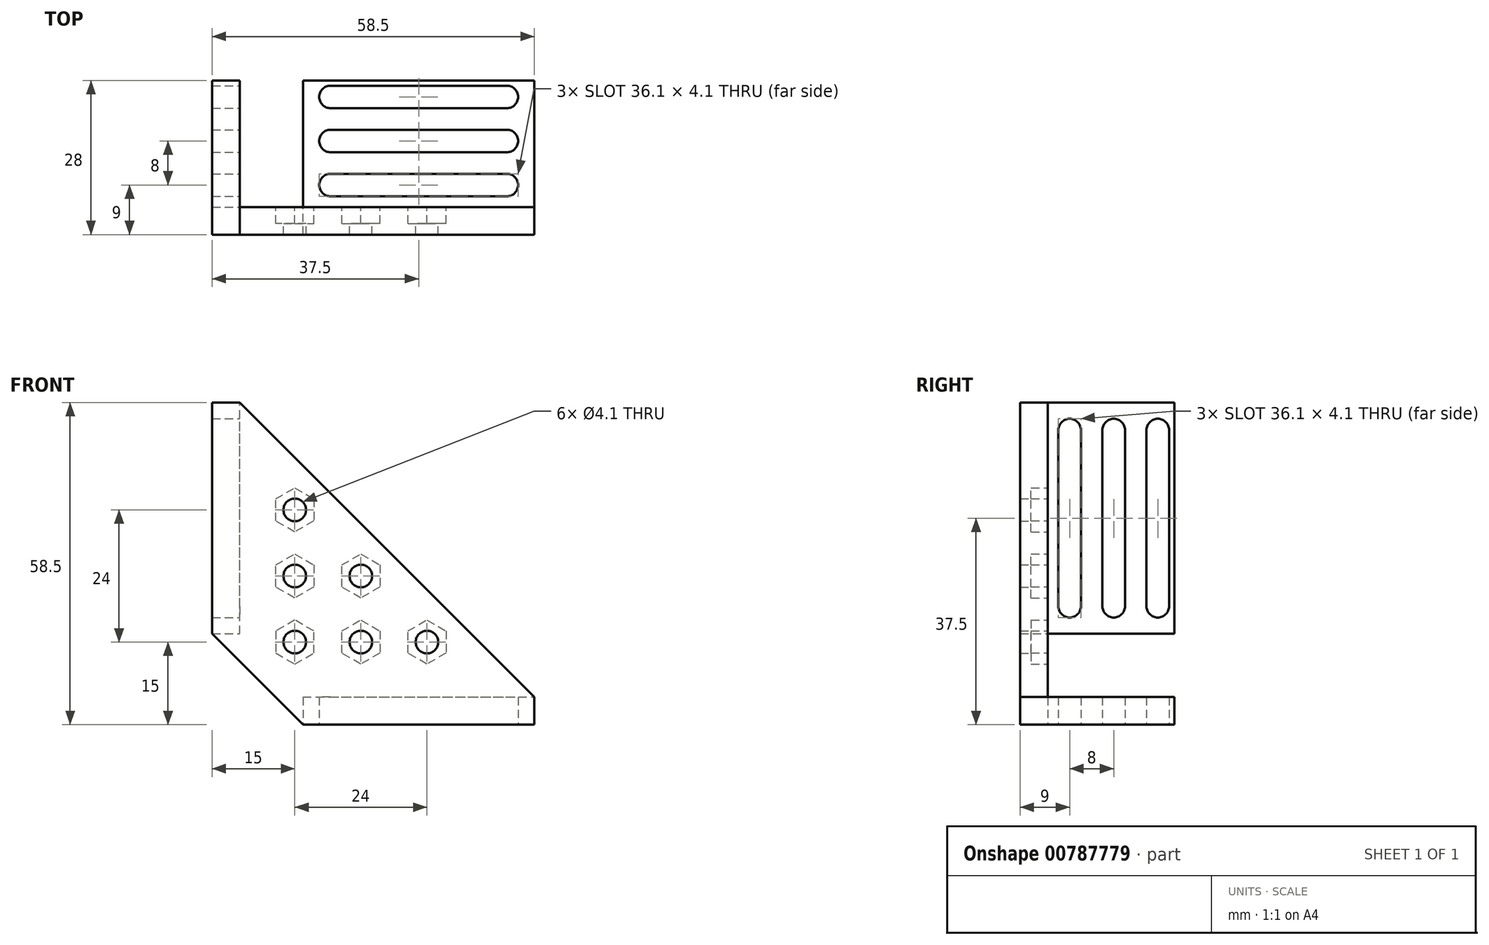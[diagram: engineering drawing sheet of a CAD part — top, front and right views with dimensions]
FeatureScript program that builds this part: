
annotation { "Feature Type Name" : "Feature", "Feature Type Description" : "" }
export const myFeature = defineFeature(function(context is Context, id is Id, definition is map)
    precondition{}
    {
        {
            var Q0;
            Q0=qCreatedBy(makeId("Top.planeOp"),FACE);
            var sketch = newSketch(context, id + "F0", { "sketchPlane" : qUnion([Q0])});
            skLineSegment(sketch, "E0.bottom", {"start": v(-21, 11.5) * mm, "end": v(21, 11.5) * mm});
            skLineSegment(sketch, "E0.top", {"start": v(-21, -11.5) * mm, "end": v(21, -11.5) * mm});
            skLineSegment(sketch, "E0.left", {"start": v(-21, 11.5) * mm, "end": v(-21, -11.5) * mm});
            skLineSegment(sketch, "E0.right", {"start": v(21, 11.5) * mm, "end": v(21, -11.5) * mm});
            skPoint(sketch, "E0.middle", {"position": v(0, 0) * mm});
            skLineSegment(sketch, "E1", {"start": v(0, 11.5) * mm, "end": v(0, -11.5) * mm, "construction": true});
            skLineSegment(sketch, "E2", {"start": v(-21, -7.5) * mm, "end": v(21, -7.5) * mm, "construction": true});
            skLineSegment(sketch, "E3", {"start": v(-16, 11.5) * mm, "end": v(-16, -11.5) * mm, "construction": true});
            skPoint(sketch, "E4", {"position": v(-16, -7.5) * mm});
            skPoint(sketch, "E5", {"position": v(0, -7.5) * mm});
            skArc(sketch, "E6", {"start": v(-16, -5.45) * mm, "mid": v(-18.05, -7.5) * mm, "end": v(-16, -9.55) * mm});
            skArc(sketch, "E7.MirrorCS", {"start": v(16, -5.45) * mm, "mid": v(18.05, -7.5) * mm, "end": v(16, -9.55) * mm});
            skLineSegment(sketch, "E8", {"start": v(-16, -5.45) * mm, "end": v(16, -5.45) * mm});
            skLineSegment(sketch, "E9", {"start": v(-16, -9.55) * mm, "end": v(16, -9.55) * mm});
            skLineSegment(sketch, "E10", {"start": v(-21, 0.5) * mm, "end": v(21, 0.5) * mm, "construction": true});
            skLineSegment(sketch, "E11.MirrorCS", {"start": v(-16, 6.45) * mm, "end": v(16, 6.45) * mm});
            skArc(sketch, "E12.MirrorCS", {"start": v(-16, 6.45) * mm, "mid": v(-18.05, 8.5) * mm, "end": v(-16, 10.55) * mm});
            skLineSegment(sketch, "E13.MirrorCS", {"start": v(-16, 10.55) * mm, "end": v(16, 10.55) * mm});
            skArc(sketch, "E14.MirrorCS", {"start": v(16, 6.45) * mm, "mid": v(18.05, 8.5) * mm, "end": v(16, 10.55) * mm});
            skPoint(sketch, "E15", {"position": v(-16, 0.5) * mm});
            skArc(sketch, "E16", {"start": v(-16, -1.55) * mm, "mid": v(-18.05, 0.5) * mm, "end": v(-16, 2.55) * mm});
            skLineSegment(sketch, "E17", {"start": v(-16, -1.55) * mm, "end": v(0, -1.55) * mm});
            skLineSegment(sketch, "E18", {"start": v(-16, 2.55) * mm, "end": v(0, 2.55) * mm});
            skLineSegment(sketch, "E19.MirrorCS", {"start": v(16, 2.55) * mm, "end": v(0, 2.55) * mm});
            skLineSegment(sketch, "E20.MirrorCS", {"start": v(16, -1.55) * mm, "end": v(0, -1.55) * mm});
            skArc(sketch, "E21.MirrorCS", {"start": v(16, -1.55) * mm, "mid": v(18.05, 0.5) * mm, "end": v(16, 2.55) * mm});
            skSolve(sketch);
        }
        {
            var Q0;
            Q0=makeQuery(id+"F0.imprint","IMPRINT",FACE,{"disambiguationData":[TD([[makeQuery(id+"F0.imprint","IMPRINT",EDGE,{"derivedFrom":sQuery(id+"F0.wireOp",EDGE,"E0.bottom")}),-1.0]])]});
            extrude(context, id + "F1", {"entities" : qUnion([Q0]), "depth" : 5 * mm, "offsetDistance" : 25 * mm});
        }
        {
            var Q0;
            Q0=makeQuery(id+"F1.opExtrude","SWEPT_FACE",FACE,{"disambiguationData":[OSD([sQuery(id+"F0.wireOp",EDGE,"E0.left")])]});
            var sketch = newSketch(context, id + "F2", { "sketchPlane" : qUnion([Q0])});
            skLineSegment(sketch, "E22", {"start": v(-11.5, 2.5) * mm, "end": v(11.5, 2.5) * mm, "construction": true});
            skSolve(sketch);
        }
        {
            var Q0;
            Q0=makeQuery(id+"F1.opExtrude","SWEPT_BODY",BODY,{"disambiguationData":[OSD([sQuery(id+"F0.wireOp",EDGE,"E0.bottom"),sQuery(id+"F0.wireOp",EDGE,"E0.top"),sQuery(id+"F0.wireOp",EDGE,"E0.left"),sQuery(id+"F0.wireOp",EDGE,"E0.right"),sQuery(id+"F0.wireOp",EDGE,"rf366HtQ-3S43-huQP-rZQL-GLvETnePYKPt"),sQuery(id+"F0.wireOp",EDGE,"72d57c59-205e-4b86-9b7f-fefa83471a3c0.MirrorC"),sQuery(id+"F0.wireOp",EDGE,"3BxVGwLA-TLUy-tZVP-cH0U-NxRYkcQ5ksQi"),sQuery(id+"F0.wireOp",EDGE,"b526d6a5-a937-4610-9a53-f8e406b30c9d0.MirrorC"),sQuery(id+"F0.wireOp",EDGE,"71981b63-6e51-433c-862b-60b74b25135c0.MirrorC"),sQuery(id+"F0.wireOp",EDGE,"b5f8f83e-67df-48da-9f18-6f8bbd20fa1b0.MirrorC"),sQuery(id+"F0.wireOp",EDGE,"1DxgEhBs-8iCY-IMLj-HmtB-05ri525AO9wY"),sQuery(id+"F0.wireOp",EDGE,"NxLUD5A4-VjtB-lD8M-x3iM-VxBEk0lLSaKk"),sQuery(id+"F0.wireOp",EDGE,"3f1f5e11-1e70-4af8-87df-d7b5c765f6460.MirrorC")])]});
            var Q1;
            Q1=sQuery(id+"F2.wireOp",EDGE,"E22");
            transform(context, id + "F3", {"entities" : qUnion([Q0]), "transformType" : TransformType.ROTATION, "transformAxis" : qUnion([Q1]), "angle" : 90 * degree, "makeCopy" : true});
        }
        {
            var Q0;
            Q0=makeQuery(id+"F3.opPattern","COPY",BODY,{"derivedFrom":makeQuery(id+"F1.opExtrude","SWEPT_BODY",BODY,{"disambiguationData":[OSD([sQuery(id+"F0.wireOp",EDGE,"E0.bottom"),sQuery(id+"F0.wireOp",EDGE,"E0.top"),sQuery(id+"F0.wireOp",EDGE,"E0.left"),sQuery(id+"F0.wireOp",EDGE,"E0.right"),sQuery(id+"F0.wireOp",EDGE,"rf366HtQ-3S43-huQP-rZQL-GLvETnePYKPt"),sQuery(id+"F0.wireOp",EDGE,"72d57c59-205e-4b86-9b7f-fefa83471a3c0.MirrorC"),sQuery(id+"F0.wireOp",EDGE,"3BxVGwLA-TLUy-tZVP-cH0U-NxRYkcQ5ksQi"),sQuery(id+"F0.wireOp",EDGE,"b526d6a5-a937-4610-9a53-f8e406b30c9d0.MirrorC"),sQuery(id+"F0.wireOp",EDGE,"71981b63-6e51-433c-862b-60b74b25135c0.MirrorC"),sQuery(id+"F0.wireOp",EDGE,"b5f8f83e-67df-48da-9f18-6f8bbd20fa1b0.MirrorC"),sQuery(id+"F0.wireOp",EDGE,"1DxgEhBs-8iCY-IMLj-HmtB-05ri525AO9wY"),sQuery(id+"F0.wireOp",EDGE,"NxLUD5A4-VjtB-lD8M-x3iM-VxBEk0lLSaKk"),sQuery(id+"F0.wireOp",EDGE,"3f1f5e11-1e70-4af8-87df-d7b5c765f6460.MirrorC")])]}),"instanceName":"1"});
            var Q1;
            Q1=qCreatedBy(makeId("Top.planeOp"),FACE);
            transform(context, id + "F4", {"entities" : qUnion([Q0]), "transformType" : TransformType.TRANSLATION_DISTANCE, "transformDirection" : qUnion([Q1]), "distance" : 14 * mm, "makeCopy" : false});
        }
        {
            var Q0;
            Q0=makeQuery(id+"F3.opPattern","COPY",BODY,{"derivedFrom":makeQuery(id+"F1.opExtrude","SWEPT_BODY",BODY,{"disambiguationData":[OSD([sQuery(id+"F0.wireOp",EDGE,"E0.bottom"),sQuery(id+"F0.wireOp",EDGE,"E0.top"),sQuery(id+"F0.wireOp",EDGE,"E0.left"),sQuery(id+"F0.wireOp",EDGE,"E0.right"),sQuery(id+"F0.wireOp",EDGE,"rf366HtQ-3S43-huQP-rZQL-GLvETnePYKPt"),sQuery(id+"F0.wireOp",EDGE,"72d57c59-205e-4b86-9b7f-fefa83471a3c0.MirrorC"),sQuery(id+"F0.wireOp",EDGE,"3BxVGwLA-TLUy-tZVP-cH0U-NxRYkcQ5ksQi"),sQuery(id+"F0.wireOp",EDGE,"b526d6a5-a937-4610-9a53-f8e406b30c9d0.MirrorC"),sQuery(id+"F0.wireOp",EDGE,"71981b63-6e51-433c-862b-60b74b25135c0.MirrorC"),sQuery(id+"F0.wireOp",EDGE,"b5f8f83e-67df-48da-9f18-6f8bbd20fa1b0.MirrorC"),sQuery(id+"F0.wireOp",EDGE,"1DxgEhBs-8iCY-IMLj-HmtB-05ri525AO9wY"),sQuery(id+"F0.wireOp",EDGE,"NxLUD5A4-VjtB-lD8M-x3iM-VxBEk0lLSaKk"),sQuery(id+"F0.wireOp",EDGE,"3f1f5e11-1e70-4af8-87df-d7b5c765f6460.MirrorC")])]}),"instanceName":"1"});
            var Q1;
            Q1=qCreatedBy(makeId("Right.planeOp"),FACE);
            transform(context, id + "F5", {"entities" : qUnion([Q0]), "transformType" : TransformType.TRANSLATION_DISTANCE, "transformDirection" : qUnion([Q1]), "distance" : 14 * mm, "oppositeDirection" : true, "makeCopy" : false});
        }
        {
            var Q0;
            Q0=makeQuery(id+"F1.opExtrude","CAP_EDGE",EDGE,{"disambiguationData":[OSD([sQuery(id+"F0.wireOp",EDGE,"E0.top")])],"isStart":false});
            cPoint(context, id + "F6", {"entities" : qUnion([Q0]), "parameter" : 0.5});
        }
        {
            var Q0;
            Q0=makeQuery(id+"F1.opExtrude","CAP_VERTEX",VERTEX,{"disambiguationData":[OSD([sQuery(id+"F0.wireOp",EDGE,"E0.top"),sQuery(id+"F0.wireOp",EDGE,"E0.left")])],"isStart":true});
            var Q1;
            Q1=makeQuery(id+"F3.opPattern","COPY",VERTEX,{"derivedFrom":makeQuery(id+"F1.opExtrude","CAP_VERTEX",VERTEX,{"disambiguationData":[OSD([sQuery(id+"F0.wireOp",EDGE,"E0.top"),sQuery(id+"F0.wireOp",EDGE,"E0.left")])],"isStart":true}),"instanceName":"1"});
            var Q2;
            Q2=qCreatedBy(id+"F6",VERTEX);
            cPlane(context, id + "F7", {"entities" : qUnion([Q0, Q1, Q2]), "cplaneType" : CPlaneType.THREE_POINT, "offset" : 25 * mm, "width" : 150 * mm, "height" : 150 * mm});
        }
        {
            var Q0;
            Q0=qCreatedBy(id+"F7.planeOp",FACE);
            var sketch = newSketch(context, id + "F8", { "sketchPlane" : qUnion([Q0])});
            skLineSegment(sketch, "E23", {"start": v(-21, 0) * mm, "end": v(-37.5, 16.5) * mm});
            skLineSegment(sketch, "E24", {"start": v(-32.5, 58.5) * mm, "end": v(21, 5) * mm});
            skLineSegment(sketch, "E25", {"start": v(-37.5, 16.5) * mm, "end": v(-37.5, 58.5) * mm});
            skLineSegment(sketch, "E26", {"start": v(-37.5, 58.5) * mm, "end": v(-32.5, 58.5) * mm});
            skLineSegment(sketch, "E27", {"start": v(-21, 0) * mm, "end": v(21, 0) * mm});
            skLineSegment(sketch, "E28", {"start": v(21, 0) * mm, "end": v(21, 5) * mm});
            skLineSegment(sketch, "E29", {"start": v(-32.5, 58.5) * mm, "end": v(-37.5, 58.5) * mm});
            skPoint(sketch, "E30", {"position": v(-10.5, 27) * mm});
            skCircle(sketch, "E31", {"center": v(-10.5, 27) * mm, "radius": 2.05 * mm});
            skCircle(sketch, "E32.cCircle", {"center": v(-10.5, 27) * mm, "radius": 4 * mm, "construction": true});
            skLineSegment(sketch, "E32.0", {"start": v(-13.96, 29) * mm, "end": v(-10.5, 31) * mm});
            skLineSegment(sketch, "E32.1", {"start": v(-10.5, 31) * mm, "end": v(-7.04, 29) * mm});
            skLineSegment(sketch, "E32.2", {"start": v(-7.04, 29) * mm, "end": v(-7.04, 25) * mm});
            skLineSegment(sketch, "E32.3", {"start": v(-7.04, 25) * mm, "end": v(-10.5, 23) * mm});
            skLineSegment(sketch, "E32.4", {"start": v(-10.5, 23) * mm, "end": v(-13.96, 25) * mm});
            skLineSegment(sketch, "E32.5", {"start": v(-13.96, 25) * mm, "end": v(-13.96, 29) * mm});
            skLineSegment(sketch, "E33", {"start": v(-10.5, 27) * mm, "end": v(-10.5, 5) * mm, "construction": true});
            skLineSegment(sketch, "E34", {"start": v(-10.5, 27) * mm, "end": v(-32.5, 27) * mm, "construction": true});
            skCircle(sketch, "E35", {"center": v(-22.5, 27) * mm, "radius": 2.05 * mm});
            skCircle(sketch, "E36.cCircle", {"center": v(-22.5, 27) * mm, "radius": 4 * mm, "construction": true});
            skLineSegment(sketch, "E36.0", {"start": v(-25.96, 29) * mm, "end": v(-22.5, 31) * mm});
            skLineSegment(sketch, "E36.1", {"start": v(-22.5, 31) * mm, "end": v(-19.04, 29) * mm});
            skLineSegment(sketch, "E36.2", {"start": v(-19.04, 29) * mm, "end": v(-19.04, 25) * mm});
            skLineSegment(sketch, "E36.3", {"start": v(-19.04, 25) * mm, "end": v(-22.5, 23) * mm});
            skLineSegment(sketch, "E36.4", {"start": v(-22.5, 23) * mm, "end": v(-25.96, 25) * mm});
            skLineSegment(sketch, "E36.5", {"start": v(-25.96, 25) * mm, "end": v(-25.96, 29) * mm});
            skLineSegment(sketch, "E37", {"start": v(-22.5, 48.5) * mm, "end": v(-22.5, 5) * mm, "construction": true});
            skLineSegment(sketch, "E38", {"start": v(1.5, 24.5) * mm, "end": v(1.5, 5) * mm, "construction": true});
            skLineSegment(sketch, "E39", {"start": v(13.5, 12.5) * mm, "end": v(13.5, 5) * mm, "construction": true});
            skLineSegment(sketch, "E40", {"start": v(11, 15) * mm, "end": v(-32.5, 15) * mm, "construction": true});
            skLineSegment(sketch, "E41", {"start": v(-13, 39) * mm, "end": v(-32.5, 39) * mm, "construction": true});
            skPoint(sketch, "E42", {"position": v(-22.5, 39) * mm});
            skPoint(sketch, "E43", {"position": v(-10.5, 15) * mm});
            skPoint(sketch, "E44", {"position": v(1.5, 15) * mm});
            skPoint(sketch, "E45", {"position": v(13.5, 15) * mm});
            skCircle(sketch, "E46", {"center": v(-22.5, 39) * mm, "radius": 2.05 * mm});
            skCircle(sketch, "E47.cCircle", {"center": v(-22.5, 39) * mm, "radius": 4 * mm, "construction": true});
            skLineSegment(sketch, "E47.0", {"start": v(-25.96, 41) * mm, "end": v(-22.5, 43) * mm});
            skLineSegment(sketch, "E47.1", {"start": v(-22.5, 43) * mm, "end": v(-19.04, 41) * mm});
            skLineSegment(sketch, "E47.2", {"start": v(-19.04, 41) * mm, "end": v(-19.04, 37) * mm});
            skLineSegment(sketch, "E47.3", {"start": v(-19.04, 37) * mm, "end": v(-22.5, 35) * mm});
            skLineSegment(sketch, "E47.4", {"start": v(-22.5, 35) * mm, "end": v(-25.96, 37) * mm});
            skLineSegment(sketch, "E47.5", {"start": v(-25.96, 37) * mm, "end": v(-25.96, 41) * mm});
            skCircle(sketch, "E48", {"center": v(-10.5, 15) * mm, "radius": 2.05 * mm});
            skCircle(sketch, "E49.cCircle", {"center": v(-10.5, 15) * mm, "radius": 4 * mm, "construction": true});
            skLineSegment(sketch, "E49.0", {"start": v(-13.96, 17) * mm, "end": v(-10.5, 19) * mm});
            skLineSegment(sketch, "E49.1", {"start": v(-10.5, 19) * mm, "end": v(-7.04, 17) * mm});
            skLineSegment(sketch, "E49.2", {"start": v(-7.04, 17) * mm, "end": v(-7.04, 13) * mm});
            skLineSegment(sketch, "E49.3", {"start": v(-7.04, 13) * mm, "end": v(-10.5, 11) * mm});
            skLineSegment(sketch, "E49.4", {"start": v(-10.5, 11) * mm, "end": v(-13.96, 13) * mm});
            skLineSegment(sketch, "E49.5", {"start": v(-13.96, 13) * mm, "end": v(-13.96, 17) * mm});
            skCircle(sketch, "E50", {"center": v(1.5, 15) * mm, "radius": 2.05 * mm});
            skCircle(sketch, "E51.cCircle", {"center": v(1.5, 15) * mm, "radius": 4 * mm, "construction": true});
            skLineSegment(sketch, "E51.0", {"start": v(-1.96, 17) * mm, "end": v(1.5, 19) * mm});
            skLineSegment(sketch, "E51.1", {"start": v(1.5, 19) * mm, "end": v(4.96, 17) * mm});
            skLineSegment(sketch, "E51.2", {"start": v(4.96, 17) * mm, "end": v(4.96, 13) * mm});
            skLineSegment(sketch, "E51.3", {"start": v(4.96, 13) * mm, "end": v(1.5, 11) * mm});
            skLineSegment(sketch, "E51.4", {"start": v(1.5, 11) * mm, "end": v(-1.96, 13) * mm});
            skLineSegment(sketch, "E51.5", {"start": v(-1.96, 13) * mm, "end": v(-1.96, 17) * mm});
            skLineSegment(sketch, "E52", {"start": v(-29.25, 8.25) * mm, "end": v(-5.75, 31.75) * mm, "construction": true});
            skLineSegment(sketch, "E53.MirrorCS", {"start": v(1.5, 31) * mm, "end": v(-1.96, 29) * mm});
            skLineSegment(sketch, "E54.MirrorCS", {"start": v(4.96, 29) * mm, "end": v(1.5, 31) * mm});
            skLineSegment(sketch, "E55.MirrorCS", {"start": v(-1.96, 25) * mm, "end": v(1.5, 23) * mm});
            skLineSegment(sketch, "E56.MirrorCS", {"start": v(-1.96, 29) * mm, "end": v(-1.96, 25) * mm});
            skLineSegment(sketch, "E57.MirrorCS", {"start": v(1.5, 23) * mm, "end": v(4.96, 25) * mm});
            skCircle(sketch, "E58.MirrorC", {"center": v(1.5, 27) * mm, "radius": 2.05 * mm});
            skLineSegment(sketch, "E59.MirrorCS", {"start": v(4.96, 25) * mm, "end": v(4.96, 29) * mm});
            skCircle(sketch, "E60.MirrorC", {"center": v(1.5, 27) * mm, "radius": 4 * mm, "construction": true});
            skLineSegment(sketch, "E61.MirrorCS", {"start": v(-10.5, 35) * mm, "end": v(-7.04, 37) * mm});
            skLineSegment(sketch, "E62.MirrorCS", {"start": v(-7.04, 41) * mm, "end": v(-10.5, 43) * mm});
            skCircle(sketch, "E63.MirrorC", {"center": v(-10.5, 39) * mm, "radius": 2.05 * mm});
            skCircle(sketch, "E64.MirrorC", {"center": v(-10.5, 39) * mm, "radius": 4 * mm, "construction": true});
            skLineSegment(sketch, "E65.MirrorCS", {"start": v(-10.5, 43) * mm, "end": v(-13.96, 41) * mm});
            skLineSegment(sketch, "E66.MirrorCS", {"start": v(-13.96, 41) * mm, "end": v(-13.96, 37) * mm});
            skLineSegment(sketch, "E67.MirrorCS", {"start": v(-7.04, 37) * mm, "end": v(-7.04, 41) * mm});
            skLineSegment(sketch, "E68.MirrorCS", {"start": v(-13.96, 37) * mm, "end": v(-10.5, 35) * mm});
            skLineSegment(sketch, "E69.MirrorCS", {"start": v(-22.5, 47) * mm, "end": v(-19.04, 49) * mm});
            skLineSegment(sketch, "E70.MirrorCS", {"start": v(-25.96, 53) * mm, "end": v(-25.96, 49) * mm});
            skCircle(sketch, "E71.MirrorC", {"center": v(-22.5, 51) * mm, "radius": 4 * mm, "construction": true});
            skCircle(sketch, "E72.MirrorC", {"center": v(-22.5, 51) * mm, "radius": 2.05 * mm});
            skLineSegment(sketch, "E73.MirrorCS", {"start": v(-19.04, 49) * mm, "end": v(-19.04, 53) * mm});
            skLineSegment(sketch, "E74.MirrorCS", {"start": v(-10.5, 51) * mm, "end": v(-32.5, 51) * mm, "construction": true});
            skLineSegment(sketch, "E75.MirrorCS", {"start": v(-22.5, 55) * mm, "end": v(-25.96, 53) * mm});
            skLineSegment(sketch, "E76.MirrorCS", {"start": v(-22.5, 29.5) * mm, "end": v(-22.5, 73) * mm, "construction": true});
            skLineSegment(sketch, "E77.MirrorCS", {"start": v(-25.96, 49) * mm, "end": v(-22.5, 47) * mm});
            skLineSegment(sketch, "E78.MirrorCS", {"start": v(-19.04, 53) * mm, "end": v(-22.5, 55) * mm});
            skLineSegment(sketch, "E79.MirrorCS", {"start": v(13.5, 19) * mm, "end": v(10.04, 17) * mm});
            skCircle(sketch, "E80.MirrorC", {"center": v(13.5, 15) * mm, "radius": 2.05 * mm});
            skLineSegment(sketch, "E81.MirrorCS", {"start": v(13.5, 11) * mm, "end": v(16.96, 13) * mm});
            skLineSegment(sketch, "E82.MirrorCS", {"start": v(10.04, 13) * mm, "end": v(13.5, 11) * mm});
            skCircle(sketch, "E83.MirrorC", {"center": v(13.5, 15) * mm, "radius": 4 * mm, "construction": true});
            skLineSegment(sketch, "E84.MirrorCS", {"start": v(10.04, 17) * mm, "end": v(10.04, 13) * mm});
            skLineSegment(sketch, "E85.MirrorCS", {"start": v(16.96, 13) * mm, "end": v(16.96, 17) * mm});
            skLineSegment(sketch, "E86.MirrorCS", {"start": v(16.96, 17) * mm, "end": v(13.5, 19) * mm});
            skLineSegment(sketch, "E87", {"start": v(-37.5, 16.5) * mm, "end": v(-37.5, 0) * mm, "construction": true});
            skLineSegment(sketch, "E88", {"start": v(-37.5, 0) * mm, "end": v(-21, 0) * mm, "construction": true});
            skLineSegment(sketch, "E89", {"start": v(-32.5, 16.5) * mm, "end": v(-32.5, 5) * mm, "construction": true});
            skLineSegment(sketch, "E90", {"start": v(-32.5, 5) * mm, "end": v(-21, 5) * mm, "construction": true});
            skLineSegment(sketch, "E91.MirrorCS", {"start": v(-22.5, 19) * mm, "end": v(-25.96, 17) * mm});
            skLineSegment(sketch, "E92.MirrorCS", {"start": v(-25.96, 17) * mm, "end": v(-25.96, 13) * mm});
            skLineSegment(sketch, "E93.MirrorCS", {"start": v(-22.5, 11) * mm, "end": v(-19.04, 13) * mm});
            skCircle(sketch, "E94.MirrorC", {"center": v(-22.5, 15) * mm, "radius": 2.05 * mm});
            skLineSegment(sketch, "E95.MirrorCS", {"start": v(-25.96, 13) * mm, "end": v(-22.5, 11) * mm});
            skLineSegment(sketch, "E96.MirrorCS", {"start": v(-19.04, 13) * mm, "end": v(-19.04, 17) * mm});
            skCircle(sketch, "E97.MirrorC", {"center": v(-22.5, 15) * mm, "radius": 4 * mm, "construction": true});
            skLineSegment(sketch, "E98.MirrorCS", {"start": v(-19.04, 17) * mm, "end": v(-22.5, 19) * mm});
            skSolve(sketch);
        }
        {
            var Q0;
            Q0=makeQuery(id+"F8.imprint","IMPRINT",FACE,{"disambiguationData":[TD([[makeQuery(id+"F8.imprint","IMPRINT",EDGE,{"derivedFrom":sQuery(id+"F8.wireOp",EDGE,"E24")}),-1.0]])]});
            var Q1;
            Q1=makeQuery(id+"F8.imprint","IMPRINT",FACE,{"disambiguationData":[TD([[makeQuery(id+"F8.imprint","IMPRINT",EDGE,{"derivedFrom":sQuery(id+"F8.wireOp",EDGE,"E46")}),-1.0]])]});
            var Q2;
            Q2=makeQuery(id+"F8.imprint","IMPRINT",FACE,{"disambiguationData":[TD([[makeQuery(id+"F8.imprint","IMPRINT",EDGE,{"derivedFrom":sQuery(id+"F8.wireOp",EDGE,"E35")}),-1.0]])]});
            var Q3;
            Q3=makeQuery(id+"F8.imprint","IMPRINT",FACE,{"disambiguationData":[TD([[makeQuery(id+"F8.imprint","IMPRINT",EDGE,{"derivedFrom":sQuery(id+"F8.wireOp",EDGE,"E31")}),-1.0]])]});
            var Q4;
            Q4=makeQuery(id+"F8.imprint","IMPRINT",FACE,{"disambiguationData":[TD([[makeQuery(id+"F8.imprint","IMPRINT",EDGE,{"derivedFrom":sQuery(id+"F8.wireOp",EDGE,"E48")}),-1.0]])]});
            var Q5;
            Q5=makeQuery(id+"F8.imprint","IMPRINT",FACE,{"disambiguationData":[TD([[makeQuery(id+"F8.imprint","IMPRINT",EDGE,{"derivedFrom":sQuery(id+"F8.wireOp",EDGE,"E50")}),-1.0]])]});
            var Q6;
            {var subQ0=sQuery(id+"F8.wireOp",EDGE,"36f95dd1-a930-4b05-802e-2328d4aa170c.1");Q6=makeQuery(id+"F8.imprint","IMPRINT",FACE,{"disambiguationData":[TD([[makeQuery(id+"F8.imprint","IMPRINT",EDGE,{"derivedFrom":subQ0}),-1.0]])]});}
            var Q7;
            Q7=makeQuery(id+"F8.imprint","IMPRINT",FACE,{"disambiguationData":[TD([[makeQuery(id+"F8.imprint","IMPRINT",EDGE,{"derivedFrom":sQuery(id+"F8.wireOp",EDGE,"E61.MirrorCS")}),1.0]])]});
            var Q8;
            Q8=makeQuery(id+"F8.imprint","IMPRINT",FACE,{"disambiguationData":[TD([[makeQuery(id+"F8.imprint","IMPRINT",EDGE,{"derivedFrom":sQuery(id+"F8.wireOp",EDGE,"E69.MirrorCS")}),1.0]])]});
            var Q9;
            Q9=makeQuery(id+"F8.imprint","IMPRINT",FACE,{"disambiguationData":[TD([[makeQuery(id+"F8.imprint","IMPRINT",EDGE,{"derivedFrom":sQuery(id+"F8.wireOp",EDGE,"E23")}),-1.0]])]});
            var Q10;
            {var subQ0=sQuery(id+"F8.wireOp",EDGE,"E82.MirrorCS");Q10=makeQuery(id+"F8.imprint","IMPRINT",FACE,{"disambiguationData":[TD([[makeQuery(id+"F8.imprint","IMPRINT",EDGE,{"derivedFrom":subQ0}),1.0]])]});}
            var Q11;
            {var subQ1=sQuery(id+"F8.wireOp",EDGE,"E55.MirrorCS");Q11=makeQuery(id+"F8.imprint","IMPRINT",FACE,{"disambiguationData":[TD([[makeQuery(id+"F8.imprint","IMPRINT",EDGE,{"derivedFrom":subQ1}),1.0]])]});}
            var Q12;
            Q12=makeQuery(id+"F8.imprint","IMPRINT",FACE,{"disambiguationData":[TD([[makeQuery(id+"F8.imprint","IMPRINT",EDGE,{"derivedFrom":sQuery(id+"F8.wireOp",EDGE,"E91.MirrorCS")}),1.0]])]});
            extrude(context, id + "F9", {"entities" : qUnion([Q0, Q1, Q2, Q3, Q4, Q5, Q6, Q7, Q8, Q9, Q10, Q11, Q12]), "operationType" : NewBodyOperationType.ADD, "depth" : 5 * mm, "offsetDistance" : 25 * mm});
        }
        {
            var Q0;
            Q0=makeQuery(id+"F8.imprint","IMPRINT",FACE,{"disambiguationData":[TD([[makeQuery(id+"F8.imprint","IMPRINT",EDGE,{"derivedFrom":sQuery(id+"F8.wireOp",EDGE,"E31")}),-1.0]])]});
            var Q1;
            Q1=makeQuery(id+"F8.imprint","IMPRINT",FACE,{"disambiguationData":[TD([[makeQuery(id+"F8.imprint","IMPRINT",EDGE,{"derivedFrom":sQuery(id+"F8.wireOp",EDGE,"E35")}),-1.0]])]});
            var Q2;
            Q2=makeQuery(id+"F8.imprint","IMPRINT",FACE,{"disambiguationData":[TD([[makeQuery(id+"F8.imprint","IMPRINT",EDGE,{"derivedFrom":sQuery(id+"F8.wireOp",EDGE,"E46")}),-1.0]])]});
            var Q3;
            Q3=makeQuery(id+"F8.imprint","IMPRINT",FACE,{"disambiguationData":[TD([[makeQuery(id+"F8.imprint","IMPRINT",EDGE,{"derivedFrom":sQuery(id+"F8.wireOp",EDGE,"a7fd36b7-951d-469d-bd4a-abdf8a5abec4")}),-1.0]])]});
            var Q4;
            Q4=makeQuery(id+"F8.imprint","IMPRINT",FACE,{"disambiguationData":[TD([[makeQuery(id+"F8.imprint","IMPRINT",EDGE,{"derivedFrom":sQuery(id+"F8.wireOp",EDGE,"E48")}),-1.0]])]});
            var Q5;
            Q5=makeQuery(id+"F8.imprint","IMPRINT",FACE,{"disambiguationData":[TD([[makeQuery(id+"F8.imprint","IMPRINT",EDGE,{"derivedFrom":sQuery(id+"F8.wireOp",EDGE,"E50")}),-1.0]])]});
            var Q6;
            Q6=makeQuery(id+"F8.imprint","IMPRINT",FACE,{"disambiguationData":[TD([[makeQuery(id+"F8.imprint","IMPRINT",EDGE,{"derivedFrom":sQuery(id+"F8.wireOp",EDGE,"E53.MirrorCS")}),1.0]])]});
            var Q7;
            Q7=makeQuery(id+"F8.imprint","IMPRINT",FACE,{"disambiguationData":[TD([[makeQuery(id+"F8.imprint","IMPRINT",EDGE,{"derivedFrom":sQuery(id+"F8.wireOp",EDGE,"E79.MirrorCS")}),1.0]])]});
            var Q8;
            Q8=makeQuery(id+"F8.imprint","IMPRINT",FACE,{"disambiguationData":[TD([[makeQuery(id+"F8.imprint","IMPRINT",EDGE,{"derivedFrom":sQuery(id+"F8.wireOp",EDGE,"E91.MirrorCS")}),1.0]])]});
            extrude(context, id + "F10", {"entities" : qUnion([Q0, Q1, Q2, Q3, Q4, Q5, Q6, Q7, Q8]), "operationType" : NewBodyOperationType.REMOVE, "depth" : 3 * mm, "offsetDistance" : 25 * mm});
        }
    });
